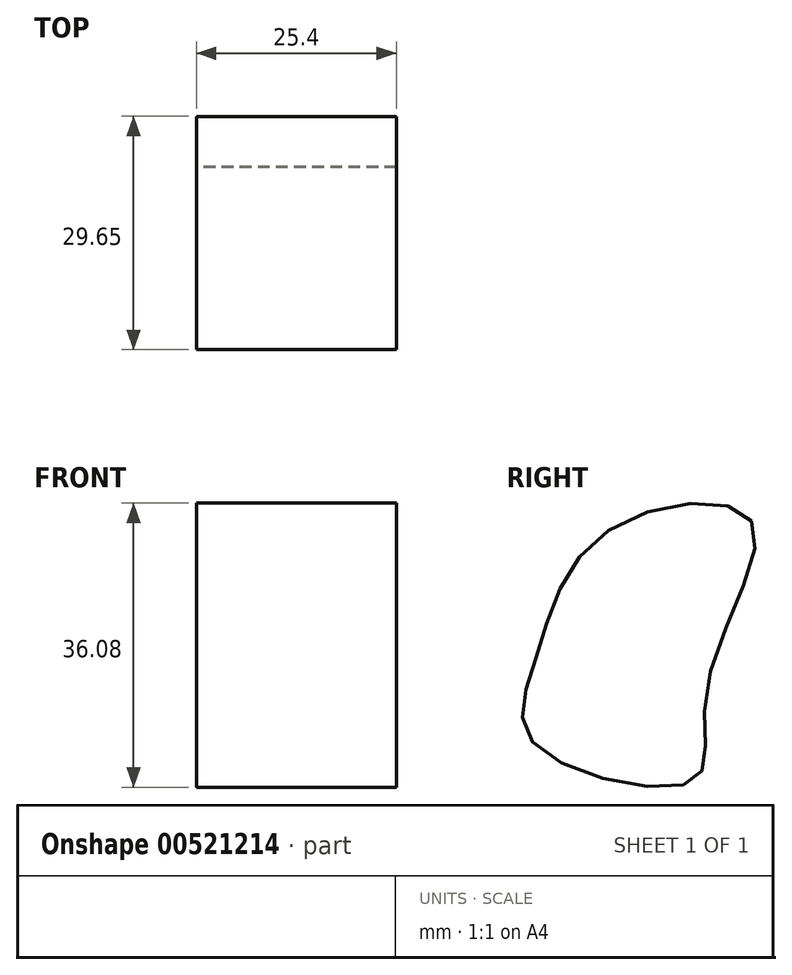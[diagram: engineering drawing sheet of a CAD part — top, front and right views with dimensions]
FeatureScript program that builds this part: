
annotation { "Feature Type Name" : "Feature", "Feature Type Description" : "" }
export const myFeature = defineFeature(function(context is Context, id is Id, definition is map)
    precondition{}
    {
        {
            var Q0;
            Q0=qCreatedBy(makeId("Right.planeOp"),FACE);
            var sketch = newSketch(context, id + "F0", { "sketchPlane" : qUnion([Q0])});
            skFitSpline(sketch, "E0", {"points": [v(12.68, 15.28) * mm, v(7, -5.75) * mm, v(5.23, -17.74) * mm, v(-14.8, -13.18) * mm, v(-14.8, -2.4) * mm, v(-5.45, 14.13) * mm, v(12.68, 15.28) * mm]});
            skSolve(sketch);
        }
        {
            var Q0;
            Q0 = qSketchRegion(id + "F0", true);
            extrude(context, id + "F1", {"entities" : qUnion([Q0]), "depth" : 25.4 * mm, "offsetDistance" : 25.4 * mm});
        }
    });
